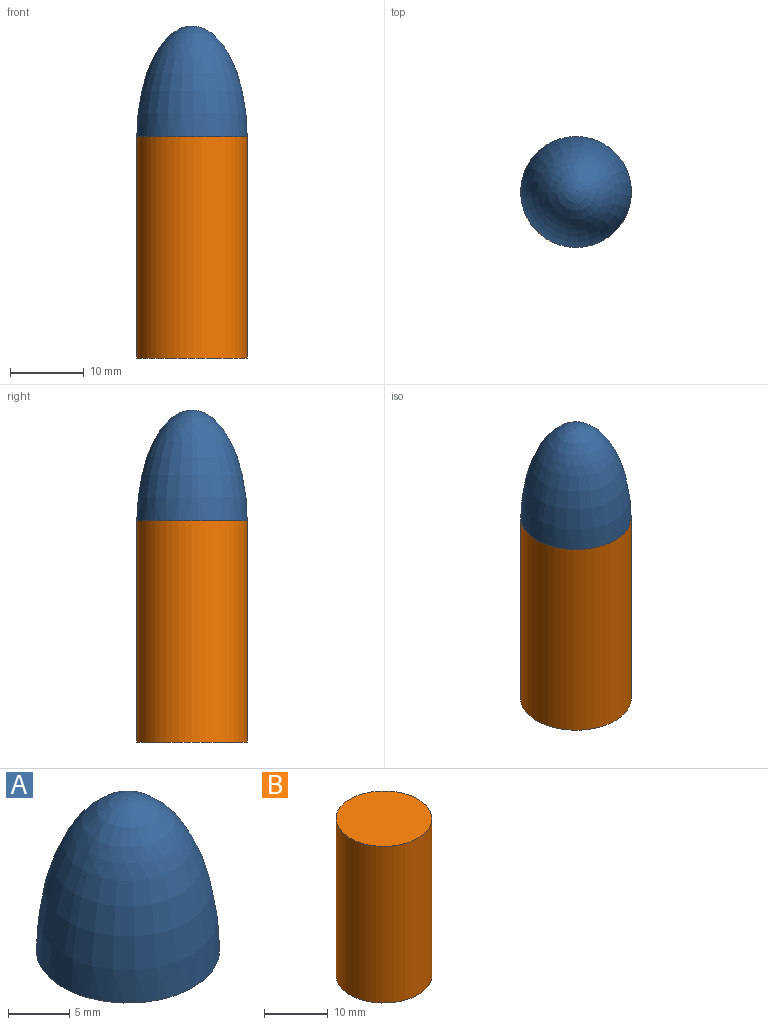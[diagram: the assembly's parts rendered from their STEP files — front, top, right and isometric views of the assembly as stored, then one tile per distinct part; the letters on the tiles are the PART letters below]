
ASSEMBLY  parts=2 mates=1
PART A: 2 faces, bbox 44.9x44.9x29.9 mm
  f0: plane 44.9x44.9mm, normal (0,0,-1), area 176mm2, adj f1
  f1: revolved ~14.97x7.48mm, area 0mm2, adj f0
PART B: 3 faces, bbox 15x15x30 mm
  f0: cylinder r=7.5mm len=30mm, axis (0,0,-1), area 1413.7mm2, adj f1,f2
  f1: plane 15x15mm, normal (0,0,1), area 176.7mm2, adj f0
  f2: plane 15x15mm, normal (0,0,-1), area 176.7mm2, adj f0
PLACE A at identity
PLACE B at identity
MATE fastened A.f0 <-> B.f0  axis (0,0,-1) through (-7.5,0,30)mm
